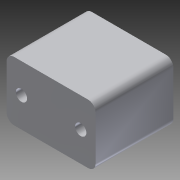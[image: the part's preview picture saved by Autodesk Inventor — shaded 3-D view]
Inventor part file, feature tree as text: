
AUTODESK INVENTOR PART (.ipt)
format: ipt  version: 2014 (Build 180170000, 170)  size: 93,184 bytes
history: native  units: in
note: dims shown in document units (in); Inventor stores cm internally (conversion verified against a paired STEP export)
features: extrude x1, sketch x1
ambient origin geometry x8: Origin, YZ Plane, XZ Plane, XY Plane, X Axis, Y Axis, Z Axis, Center Point
bodies: Solid1 (feature_tree)
feature tree (2):
  extrude  "Extrusion1"  Depth=1.0in
  sketch  "Sketch1"  dims[d0=1.5in d1=1.0in d2=0.19in d3=0.25in d5=0.7874in d7=1.0in d8=0.3937in d10=1.0in d20=0.125in d21=1.3125in d22=0.0in]
